# Revit family: HP DXE R2000
name_source: partatom
category: Mechanical Equipment
revit_build: Autodesk Revit 2015 (Build: 20140606_1530(x64)
units: mm (PartAtom-declared; Revit-internal decimal feet)

## types (4) — shared parameters
Air volume@(m3/h) high = 2560
Air volume@(m3/h) low = 1500
Air volume@(m3/h) medium = 2120
Colour = white standed RAL 9010 unless customer requests a different colour
Effective width of air stream = 2270
Electrical loading (A) = 1.4 or (14.4)*
ISO 27327 uniformity at outlet = 90%
Manufacturer = Thermoscreens ltd
Material = Sheet steel
Max.DX heat output = 15.7 with P140 unit
Maxium likely condensate flow rate (litres/hours) = 9.0
Meathordf of measurement = mm unless stated otherwise in the parameters
Model = HP DXE 2000R VRF
Noise level @ 3m high = 58
Noise level @ 3m low = 46
Noise level @ 3m medium = 53
Number of hanging points = 5
Product URL = http://www.thermoscreens.com
Rated current (A) = 1.6
Rated electrical  power input (kW) = 0.4
Status of air curtain = Brand new
Temperture classification = Low temperature
URL = http://www.thermoscreens.com
Version = 1.0
Weight/Mass = 93kg
half length = 1197 mm
half width = 270 mm
length = 2393 mm  [stored 7.85105 ft]
width = 539 mm  [stored 1.76837 ft]

## per-type parameters (varying)
| type | Fans | Max heat output (kW) | Max. cooling output (kW) | Maximum air vloume flow rate (m3/H) |
| HP DXE 2000R VRF EC | AC fans | 15.8 | 14.1 | 3200 |
| HP DXE 2000R VRF AC | EC fans | 15.7 | 14.0 | 2590 |
| HP DXE 2000R MR SLIM AC | AC fans | 15.7 | 14.0 | 2590 |
| HP DXE 2000R MR SLIM EC | AC fans | 15.8 | 14.1 | 3200 |

note: [stored X ft] marks values corroborated as IEEE doubles in the binary element streams (Revit-internal decimal feet)

## geometry (parser evidence)
native form markers: Sweep x2
no freeform markers — native parametric forms only
